# Revit family: Plumbing_Drainage_DURAVIT-AG_Design-siphon-Bronze-Brushed-005036_NEW
name_source: partatom
category: Plumbing Fixtures
units: mm (PartAtom-declared; Revit-internal decimal feet)

## family parameters
Cut with Voids When Loaded = No
Host = Face
Maintain Annotation Orientation = No
OmniClass Number = 23.31.13.17.13
OmniClass Title = Sink Drains
Part Type = Normal
Room Calculation Point = No
Round Connector Dimension = Use Diameter
Shared = No

## types (5) — shared parameters
Description = Duravit  Design siphon Bronze Brushed Material: Brass Outlet drain: horizontal Suitable for Washbasin - 0050360400
Diameter = 32 mm  [stored 0.104987 ft]
Height = 311 mm  [stored 1.02034 ft]
Installation instructions = https://duravit-public-assets.s3.eu-central-1.amazonaws.com
Manufacturer = Duravit
Model = Design siphon - 005036
Product Documentation Link = https://pro.duravit.com
Product Page URL = https://pro.duravit.com
Product certification = http://pro.duravit.com
Product data url = https://bimobject.com
URL = https://www.duravit.com
Version = 1
Weight = 1.50 kg
Width = 70 mm  [stored 0.229659 ft]
zero-valued in all types: Default Elevation

## per-type parameters (varying)
| type | Article Number | Material 1 |
| 10 - Chrome - 70x311 | 0050361000 | Duravit - Metal - 10 - Chrome |
| 46 - Black Matt - 70x311 | 0050364600 | Duravit - Metal - 46 - Black Matt |
| 34 - Polished Gold - 70x311 | 0050363400 | Duravit - Metal - 34 - Polished Gold |
| 04 - Brushed Bronze - 70x311 | 0050360400 | Duravit - Metal - 04 - Brushed Bronze |
| 70 - Brushed Stainless Steel - 70x311 | 0050367000 | Duravit - Metal - 70 - Brushed Stainless Steel |

note: [stored X ft] marks values corroborated as IEEE doubles in the binary element streams (Revit-internal decimal feet)

## geometry (parser evidence)
native form markers: Sweep x1
no freeform markers — native parametric forms only
